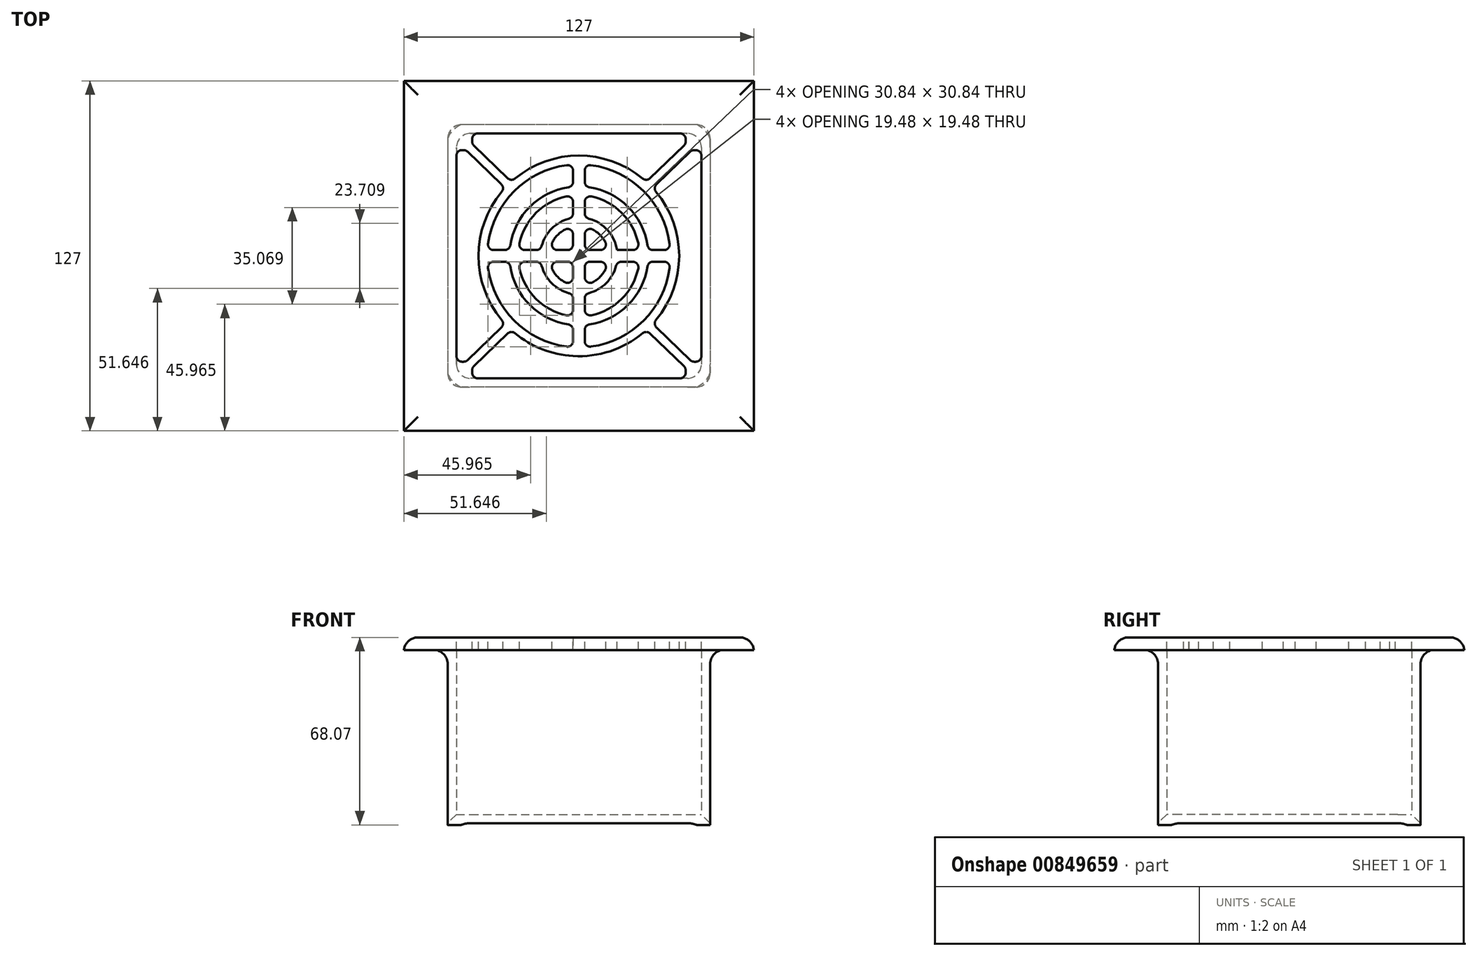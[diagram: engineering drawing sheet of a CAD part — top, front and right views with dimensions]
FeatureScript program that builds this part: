
annotation { "Feature Type Name" : "Feature", "Feature Type Description" : "" }
export const myFeature = defineFeature(function(context is Context, id is Id, definition is map)
    precondition{}
    {
        {
            var Q0;
            Q0=qCreatedBy(makeId("Top.planeOp"),FACE);
            var sketch = newSketch(context, id + "F0", { "sketchPlane" : qUnion([Q0])});
            skLineSegment(sketch, "E0.bottom", {"start": v(44.45, 44.45) * mm, "end": v(-44.45, 44.45) * mm});
            skLineSegment(sketch, "E0.top", {"start": v(44.45, -44.45) * mm, "end": v(-44.45, -44.45) * mm});
            skLineSegment(sketch, "E0.left", {"start": v(44.45, 44.45) * mm, "end": v(44.45, -44.45) * mm});
            skLineSegment(sketch, "E0.right", {"start": v(-44.45, 44.45) * mm, "end": v(-44.45, -44.45) * mm});
            skPoint(sketch, "E0.middle", {"position": v(0, 0) * mm});
            skLineSegment(sketch, "E1.0", {"start": v(47.63, 47.62) * mm, "end": v(-47.62, 47.62) * mm});
            skLineSegment(sketch, "E1.1", {"start": v(47.63, 47.62) * mm, "end": v(47.63, -47.62) * mm});
            skLineSegment(sketch, "E1.2", {"start": v(47.63, -47.62) * mm, "end": v(-47.62, -47.62) * mm});
            skLineSegment(sketch, "E1.3", {"start": v(-47.62, 47.62) * mm, "end": v(-47.62, -47.62) * mm});
            skSolve(sketch);
        }
        {
            var Q0;
            Q0=makeQuery(id+"F0.imprint","IMPRINT",FACE,{"disambiguationData":[TD([[makeQuery(id+"F0.imprint","IMPRINT",EDGE,{"derivedFrom":sQuery(id+"F0.wireOp",EDGE,"E0.bottom")}),-1.0]])]});
            extrude(context, id + "F1", {"entities" : qUnion([Q0]), "depth" : 63.5 * mm, "offsetDistance" : 25.4 * mm});
        }
        {
            var Q0;
            Q0=makeQuery(id+"F1.opExtrude","CAP_FACE",FACE,{"disambiguationData":[OSD([sQuery(id+"F0.wireOp",EDGE,"E0.bottom"),sQuery(id+"F0.wireOp",EDGE,"E0.top"),sQuery(id+"F0.wireOp",EDGE,"E0.left"),sQuery(id+"F0.wireOp",EDGE,"E0.right"),sQuery(id+"F0.wireOp",EDGE,"E1.0"),sQuery(id+"F0.wireOp",EDGE,"E1.1"),sQuery(id+"F0.wireOp",EDGE,"E1.2"),sQuery(id+"F0.wireOp",EDGE,"E1.3")])],"isStart":false});
            var sketch = newSketch(context, id + "F2", { "sketchPlane" : qUnion([Q0])});
            skLineSegment(sketch, "E2.bottom", {"start": v(63.5, 63.5) * mm, "end": v(-63.5, 63.5) * mm});
            skLineSegment(sketch, "E2.top", {"start": v(63.5, -63.5) * mm, "end": v(-63.5, -63.5) * mm});
            skLineSegment(sketch, "E2.left", {"start": v(63.5, 63.5) * mm, "end": v(63.5, -63.5) * mm});
            skLineSegment(sketch, "E2.right", {"start": v(-63.5, 63.5) * mm, "end": v(-63.5, -63.5) * mm});
            skPoint(sketch, "E2.middle", {"position": v(0, 0) * mm});
            skSolve(sketch);
        }
        {
            var Q0;
            Q0 = qSketchRegion(id + "F2", true);
            extrude(context, id + "F3", {"entities" : qUnion([Q0]), "operationType" : NewBodyOperationType.ADD, "depth" : 4.57 * mm, "offsetDistance" : 25.4 * mm});
        }
        {
            var Q0;
            Q0=makeQuery(id+"F3.opExtrude","CAP_FACE",FACE,{"disambiguationData":[OSD([sQuery(id+"F2.wireOp",EDGE,"E2.bottom"),sQuery(id+"F2.wireOp",EDGE,"E2.top"),sQuery(id+"F2.wireOp",EDGE,"E2.left"),sQuery(id+"F2.wireOp",EDGE,"E2.right")])],"isStart":false});
            var sketch = newSketch(context, id + "F4", { "sketchPlane" : qUnion([Q0])});
            skPoint(sketch, "E3.middle", {"position": v(0, 0) * mm});
            skArc(sketch, "E4", {"start": v(26.78, -24.66) * mm, "mid": v(36.4, 0) * mm, "end": v(26.78, 24.66) * mm});
            skLineSegment(sketch, "E5", {"start": v(-2.12, 2.12) * mm, "end": v(-2.12, 21.92) * mm});
            skLineSegment(sketch, "E6", {"start": v(-2.12, 33.16) * mm, "end": v(-2.12, 25.1) * mm});
            skLineSegment(sketch, "E7", {"start": v(-2.12, 2.12) * mm, "end": v(-10.6, 2.12) * mm});
            skLineSegment(sketch, "E8", {"start": v(-2.12, -2.12) * mm, "end": v(-10.6, -2.12) * mm});
            skLineSegment(sketch, "E9", {"start": v(33.16, 2.12) * mm, "end": v(25.1, 2.12) * mm});
            skLineSegment(sketch, "E10", {"start": v(2.12, -2.12) * mm, "end": v(10.6, -2.12) * mm});
            skLineSegment(sketch, "E11", {"start": v(36.4, -2.12) * mm, "end": v(36.35, -2.12) * mm});
            skLineSegment(sketch, "E12", {"start": v(2.12, -33.16) * mm, "end": v(2.12, -25.1) * mm});
            skLineSegment(sketch, "E13", {"start": v(-2.12, -2.12) * mm, "end": v(-2.12, -10.6) * mm});
            skLineSegment(sketch, "E14", {"start": v(-2.12, -36.4) * mm, "end": v(-2.1, -36.35) * mm});
            skLineSegment(sketch, "E15", {"start": v(2.12, 33.16) * mm, "end": v(2.12, 25.1) * mm});
            skPoint(sketch, "E16.orphan", {"position": v(0, 36.4) * mm});
            skPoint(sketch, "E17.orphan", {"position": v(36.4, 0) * mm});
            skPoint(sketch, "E18.orphan", {"position": v(-36.4, 0) * mm});
            skPoint(sketch, "E19.trimOffspring.end.orphan", {"position": v(0, -36.4) * mm});
            skArc(sketch, "E20", {"start": v(-2.12, 33.16) * mm, "mid": v(-23.5, 23.5) * mm, "end": v(-33.16, 2.12) * mm});
            skArc(sketch, "E21", {"start": v(-2.12, 25.1) * mm, "mid": v(-17.82, 17.82) * mm, "end": v(-25.1, 2.12) * mm});
            skArc(sketch, "E22", {"start": v(-2.12, 21.92) * mm, "mid": v(-15.57, 15.57) * mm, "end": v(-21.92, 2.12) * mm});
            skArc(sketch, "E23", {"start": v(-2.12, 13.83) * mm, "mid": v(-14, 0) * mm, "end": v(-2.12, -13.83) * mm});
            skPoint(sketch, "E24.orphan", {"position": v(2.12, 36.35) * mm});
            skLineSegment(sketch, "E25.trimOffspring", {"start": v(2.12, 21.92) * mm, "end": v(2.12, 13.83) * mm});
            skLineSegment(sketch, "E26.trimOffspring", {"start": v(-2.12, 21.92) * mm, "end": v(-2.12, 13.83) * mm});
            skLineSegment(sketch, "E27.trimOffspring", {"start": v(-2.12, 25.1) * mm, "end": v(-2.12, 33.16) * mm});
            skArc(sketch, "E28.trimOffspring", {"start": v(13.83, 2.12) * mm, "mid": v(9.9, 9.9) * mm, "end": v(2.12, 13.83) * mm});
            skArc(sketch, "E29.trimOffspring", {"start": v(21.92, 2.12) * mm, "mid": v(15.57, 15.57) * mm, "end": v(2.12, 21.92) * mm});
            skArc(sketch, "E30.trimOffspring", {"start": v(25.1, 2.12) * mm, "mid": v(17.82, 17.82) * mm, "end": v(2.12, 25.1) * mm});
            skArc(sketch, "E31.trimOffspring", {"start": v(33.16, 2.12) * mm, "mid": v(23.5, 23.5) * mm, "end": v(2.12, 33.16) * mm});
            skArc(sketch, "E32.trimOffspring", {"start": v(2.12, -25.1) * mm, "mid": v(17.82, -17.82) * mm, "end": v(25.1, -2.12) * mm});
            skArc(sketch, "E33.trimOffspring", {"start": v(2.12, -21.92) * mm, "mid": v(15.57, -15.57) * mm, "end": v(21.92, -2.12) * mm});
            skArc(sketch, "E34.trimOffspring", {"start": v(2.12, -13.83) * mm, "mid": v(9.9, -9.9) * mm, "end": v(13.83, -2.12) * mm});
            skArc(sketch, "E35.trimOffspring", {"start": v(2.12, -33.16) * mm, "mid": v(23.5, -23.5) * mm, "end": v(33.16, -2.12) * mm});
            skArc(sketch, "E36.trimOffspring", {"start": v(-33.16, -2.12) * mm, "mid": v(-23.5, -23.5) * mm, "end": v(-2.12, -33.16) * mm});
            skArc(sketch, "E37.trimOffspring", {"start": v(-25.1, -2.12) * mm, "mid": v(-17.82, -17.82) * mm, "end": v(-2.12, -25.1) * mm});
            skArc(sketch, "E38.trimOffspring", {"start": v(-21.92, -2.12) * mm, "mid": v(-15.57, -15.57) * mm, "end": v(-2.12, -21.92) * mm});
            skArc(sketch, "E39", {"start": v(-10.6, -2.12) * mm, "mid": v(0, -10.82) * mm, "end": v(10.6, -2.12) * mm});
            skArc(sketch, "E40.trimOffspring", {"start": v(10.6, 2.12) * mm, "mid": v(7.65, 7.65) * mm, "end": v(2.12, 10.6) * mm});
            skArc(sketch, "E41.trimOffspring", {"start": v(-2.12, 10.6) * mm, "mid": v(-7.65, 7.65) * mm, "end": v(-10.6, 2.12) * mm});
            skLineSegment(sketch, "E42.trimOffspring", {"start": v(2.12, 10.6) * mm, "end": v(2.12, 2.12) * mm});
            skLineSegment(sketch, "E43.trimOffspring", {"start": v(-2.12, 10.6) * mm, "end": v(-2.12, 2.12) * mm});
            skLineSegment(sketch, "E44.trimOffspring", {"start": v(-13.83, 2.12) * mm, "end": v(-21.92, 2.12) * mm});
            skLineSegment(sketch, "E45.trimOffspring", {"start": v(-13.83, -2.12) * mm, "end": v(-21.92, -2.12) * mm});
            skLineSegment(sketch, "E46.trimOffspring", {"start": v(-2.12, -13.83) * mm, "end": v(-2.12, -21.92) * mm});
            skLineSegment(sketch, "E47.trimOffspring", {"start": v(2.12, -10.6) * mm, "end": v(2.12, -2.12) * mm});
            skLineSegment(sketch, "E48.trimOffspring", {"start": v(10.6, -2.12) * mm, "end": v(2.12, -2.12) * mm});
            skLineSegment(sketch, "E49.trimOffspring", {"start": v(10.6, 2.12) * mm, "end": v(2.12, 2.12) * mm});
            skLineSegment(sketch, "E50.trimOffspring", {"start": v(-25.1, 2.12) * mm, "end": v(-33.16, 2.12) * mm});
            skLineSegment(sketch, "E51.trimOffspring", {"start": v(-25.1, -2.12) * mm, "end": v(-33.16, -2.12) * mm});
            skLineSegment(sketch, "E52.trimOffspring", {"start": v(-2.12, -25.1) * mm, "end": v(-2.12, -33.16) * mm});
            skLineSegment(sketch, "E53.trimOffspring", {"start": v(2.12, -21.92) * mm, "end": v(2.12, -13.83) * mm});
            skLineSegment(sketch, "E54.trimOffspring", {"start": v(21.92, -2.12) * mm, "end": v(13.83, -2.12) * mm});
            skLineSegment(sketch, "E55.trimOffspring", {"start": v(21.92, 2.12) * mm, "end": v(13.83, 2.12) * mm});
            skLineSegment(sketch, "E56.trimOffspring", {"start": v(25.1, -2.12) * mm, "end": v(33.16, -2.12) * mm});
            skLineSegment(sketch, "E57.trimOffspring", {"start": v(-2.12, -36.35) * mm, "end": v(-2.12, -36.4) * mm});
            skPoint(sketch, "E58.orphan", {"position": v(2.12, -36.35) * mm});
            skLineSegment(sketch, "E59.trimOffspring", {"start": v(13.83, -2.12) * mm, "end": v(21.92, -2.12) * mm});
            skLineSegment(sketch, "E60.trimOffspring", {"start": v(36.35, -2.12) * mm, "end": v(36.4, -2.12) * mm});
            skPoint(sketch, "E61.orphan", {"position": v(36.35, 2.12) * mm});
            skLineSegment(sketch, "E62.trimOffspring", {"start": v(33.16, -2.12) * mm, "end": v(25.1, -2.12) * mm});
            skLineSegment(sketch, "E63", {"start": v(-41, -38.4) * mm, "end": v(-26.78, -24.66) * mm});
            skLineSegment(sketch, "E64", {"start": v(-38.74, -40.64) * mm, "end": v(-24.53, -26.9) * mm});
            skLineSegment(sketch, "E65", {"start": v(0, 10.6) * mm, "end": v(0, -2.12) * mm, "construction": true});
            skLineSegment(sketch, "E66", {"start": v(0, 0) * mm, "end": v(9.6, 0) * mm, "construction": true});
            skLineSegment(sketch, "E67.MirrorCS", {"start": v(41, -38.4) * mm, "end": v(26.78, -24.66) * mm});
            skLineSegment(sketch, "E68.MirrorCS", {"start": v(38.74, -40.64) * mm, "end": v(24.53, -26.9) * mm});
            skLineSegment(sketch, "E69.MirrorCS", {"start": v(-38.73, 40.64) * mm, "end": v(-24.53, 26.9) * mm});
            skLineSegment(sketch, "E70.MirrorCS", {"start": v(-41, 38.4) * mm, "end": v(-26.78, 24.66) * mm});
            skLineSegment(sketch, "E71.MirrorCS", {"start": v(41, 38.4) * mm, "end": v(26.78, 24.66) * mm});
            skLineSegment(sketch, "E72.MirrorCS", {"start": v(38.74, 40.64) * mm, "end": v(24.53, 26.9) * mm});
            skArc(sketch, "E73.trimOffspring", {"start": v(-24.53, -26.9) * mm, "mid": v(0, -36.4) * mm, "end": v(24.53, -26.9) * mm});
            skArc(sketch, "E74.trimOffspring", {"start": v(-26.78, 24.66) * mm, "mid": v(-36.4, 0) * mm, "end": v(-26.78, -24.66) * mm});
            skArc(sketch, "E75.trimOffspring", {"start": v(24.53, 26.9) * mm, "mid": v(0, 36.4) * mm, "end": v(-24.53, 26.9) * mm});
            skLineSegment(sketch, "E76.bottom", {"start": v(-44.45, -44.45) * mm, "end": v(44.45, -44.45) * mm});
            skLineSegment(sketch, "E76.top", {"start": v(-44.45, 44.45) * mm, "end": v(44.45, 44.45) * mm});
            skLineSegment(sketch, "E76.left", {"start": v(-44.45, -44.45) * mm, "end": v(-44.45, 44.45) * mm});
            skLineSegment(sketch, "E76.right", {"start": v(44.45, -44.45) * mm, "end": v(44.45, 44.45) * mm});
            skLineSegment(sketch, "E77", {"start": v(38.74, -40.64) * mm, "end": v(38.74, -44.45) * mm});
            skLineSegment(sketch, "E78", {"start": v(41, -38.4) * mm, "end": v(44.45, -38.4) * mm});
            skLineSegment(sketch, "E79", {"start": v(38.74, 40.64) * mm, "end": v(38.74, 44.45) * mm});
            skLineSegment(sketch, "E80", {"start": v(41, 38.4) * mm, "end": v(44.45, 38.4) * mm});
            skLineSegment(sketch, "E81", {"start": v(-38.73, 40.64) * mm, "end": v(-38.73, 44.45) * mm});
            skLineSegment(sketch, "E82", {"start": v(-41, 38.4) * mm, "end": v(-44.45, 38.4) * mm});
            skLineSegment(sketch, "E83", {"start": v(-41, -38.4) * mm, "end": v(-44.45, -38.4) * mm});
            skLineSegment(sketch, "E84", {"start": v(-38.74, -40.64) * mm, "end": v(-38.74, -44.45) * mm});
            skSolve(sketch);
        }
        {
            var Q0;
            {var subQ2=sQuery(id+"F4.wireOp",EDGE,"E69.MirrorCS");Q0=makeQuery(id+"F4.imprint","IMPRINT",FACE,{"disambiguationData":[TD([[makeQuery(id+"F4.imprint","IMPRINT",EDGE,{"derivedFrom":subQ2}),1.0]])]});}
            var Q1;
            {var subQ0=sQuery(id+"F4.wireOp",EDGE,"E63");Q1=makeQuery(id+"F4.imprint","IMPRINT",FACE,{"disambiguationData":[TD([[makeQuery(id+"F4.imprint","IMPRINT",EDGE,{"derivedFrom":subQ0}),1.0]])]});}
            var Q2;
            Q2=makeQuery(id+"F4.imprint","IMPRINT",FACE,{"disambiguationData":[TD([[makeQuery(id+"F4.imprint","IMPRINT",EDGE,{"derivedFrom":sQuery(id+"F4.wireOp",EDGE,"E20")}),1.0]])]});
            var Q3;
            Q3=makeQuery(id+"F4.imprint","IMPRINT",FACE,{"disambiguationData":[TD([[makeQuery(id+"F4.imprint","IMPRINT",EDGE,{"derivedFrom":sQuery(id+"F4.wireOp",EDGE,"E22")}),1.0]])]});
            var Q4;
            Q4=makeQuery(id+"F4.imprint","IMPRINT",FACE,{"disambiguationData":[TD([[makeQuery(id+"F4.imprint","IMPRINT",EDGE,{"derivedFrom":sQuery(id+"F4.wireOp",EDGE,"E7")}),-1.0]])]});
            var Q5;
            Q5=makeQuery(id+"F4.imprint","IMPRINT",FACE,{"disambiguationData":[TD([[makeQuery(id+"F4.imprint","IMPRINT",EDGE,{"derivedFrom":sQuery(id+"F4.wireOp",EDGE,"E40.trimOffspring")}),1.0]])]});
            var Q6;
            {var subQ2=sQuery(id+"F4.wireOp",EDGE,"E47.trimOffspring");Q6=makeQuery(id+"F4.imprint","IMPRINT",FACE,{"disambiguationData":[TD([[makeQuery(id+"F4.imprint","IMPRINT",EDGE,{"derivedFrom":subQ2}),-1.0]])]});}
            var Q7;
            {var subQ0=sQuery(id+"F4.wireOp",EDGE,"E8");Q7=makeQuery(id+"F4.imprint","IMPRINT",FACE,{"disambiguationData":[TD([[makeQuery(id+"F4.imprint","IMPRINT",EDGE,{"derivedFrom":subQ0}),1.0]])]});}
            var Q8;
            Q8=makeQuery(id+"F4.imprint","IMPRINT",FACE,{"disambiguationData":[TD([[makeQuery(id+"F4.imprint","IMPRINT",EDGE,{"derivedFrom":sQuery(id+"F4.wireOp",EDGE,"E38.trimOffspring")}),1.0]])]});
            var Q9;
            Q9=makeQuery(id+"F4.imprint","IMPRINT",FACE,{"disambiguationData":[TD([[makeQuery(id+"F4.imprint","IMPRINT",EDGE,{"derivedFrom":sQuery(id+"F4.wireOp",EDGE,"E36.trimOffspring")}),1.0]])]});
            var Q10;
            {var subQ1=sQuery(id+"F4.wireOp",EDGE,"E14");Q10=makeQuery(id+"F4.imprint","IMPRINT",FACE,{"disambiguationData":[TD([[makeQuery(id+"F4.imprint","IMPRINT",EDGE,{"derivedFrom":subQ1}),-1.0]])]});}
            var Q11;
            Q11=makeQuery(id+"F4.imprint","IMPRINT",FACE,{"disambiguationData":[TD([[makeQuery(id+"F4.imprint","IMPRINT",EDGE,{"derivedFrom":sQuery(id+"F4.wireOp",EDGE,"E12")}),-1.0]])]});
            var Q12;
            Q12=makeQuery(id+"F4.imprint","IMPRINT",FACE,{"disambiguationData":[TD([[makeQuery(id+"F4.imprint","IMPRINT",EDGE,{"derivedFrom":sQuery(id+"F4.wireOp",EDGE,"E33.trimOffspring")}),1.0]])]});
            var Q13;
            {var subQ0=sQuery(id+"F4.wireOp",EDGE,"E67.MirrorCS");Q13=makeQuery(id+"F4.imprint","IMPRINT",FACE,{"disambiguationData":[TD([[makeQuery(id+"F4.imprint","IMPRINT",EDGE,{"derivedFrom":subQ0}),-1.0]])]});}
            var Q14;
            Q14=makeQuery(id+"F4.imprint","IMPRINT",FACE,{"disambiguationData":[TD([[makeQuery(id+"F4.imprint","IMPRINT",EDGE,{"derivedFrom":sQuery(id+"F4.wireOp",EDGE,"E9")}),-1.0]])]});
            var Q15;
            Q15=makeQuery(id+"F4.imprint","IMPRINT",FACE,{"disambiguationData":[TD([[makeQuery(id+"F4.imprint","IMPRINT",EDGE,{"derivedFrom":sQuery(id+"F4.wireOp",EDGE,"E25.trimOffspring")}),1.0]])]});
            extrude(context, id + "F5", {"entities" : qUnion([Q0, Q1, Q2, Q3, Q4, Q5, Q6, Q7, Q8, Q9, Q10, Q11, Q12, Q13, Q14, Q15]), "operationType" : NewBodyOperationType.REMOVE, "endBound" : BoundingType.THROUGH_ALL, "oppositeDirection" : true, "depth" : 25.4 * mm, "offsetDistance" : 25.4 * mm});
        }
        {
            var Q0;
            Q0=makeQuery(id+"F1.opExtrude","SWEPT_EDGE",EDGE,{"disambiguationData":[OSD([sQuery(id+"F0.wireOp",EDGE,"E1.0"),sQuery(id+"F0.wireOp",EDGE,"E1.1")])]});
            var Q1;
            Q1=makeQuery(id+"F1.opExtrude","SWEPT_EDGE",EDGE,{"disambiguationData":[OSD([sQuery(id+"F0.wireOp",EDGE,"E1.1"),sQuery(id+"F0.wireOp",EDGE,"E1.2")])]});
            var Q2;
            Q2=makeQuery(id+"F1.opExtrude","SWEPT_EDGE",EDGE,{"disambiguationData":[OSD([sQuery(id+"F0.wireOp",EDGE,"E1.0"),sQuery(id+"F0.wireOp",EDGE,"E1.3")])]});
            var Q3;
            Q3=makeQuery(id+"F3.opExtrude","CAP_EDGE",EDGE,{"disambiguationData":[OSD([sQuery(id+"F2.wireOp",EDGE,"E2.bottom")])],"isStart":false});
            var Q4;
            Q4=makeQuery(id+"F3.opExtrude","CAP_EDGE",EDGE,{"disambiguationData":[OSD([sQuery(id+"F2.wireOp",EDGE,"E2.left")])],"isStart":false});
            var Q5;
            Q5=makeQuery(id+"F3.opExtrude","CAP_EDGE",EDGE,{"disambiguationData":[OSD([sQuery(id+"F2.wireOp",EDGE,"E2.top")])],"isStart":false});
            var Q6;
            Q6=makeQuery(id+"F3.opExtrude","CAP_EDGE",EDGE,{"disambiguationData":[OSD([sQuery(id+"F2.wireOp",EDGE,"E2.right")])],"isStart":false});
            var Q7;
            Q7=makeQuery(id+"F1.opExtrude","SWEPT_EDGE",EDGE,{"disambiguationData":[OSD([sQuery(id+"F0.wireOp",EDGE,"E1.2"),sQuery(id+"F0.wireOp",EDGE,"E1.3")])]});
            var Q8;
            Q8=makeQuery(id+"F1.opExtrude","SWEPT_EDGE",EDGE,{"disambiguationData":[OSD([sQuery(id+"F0.wireOp",EDGE,"E0.bottom"),sQuery(id+"F0.wireOp",EDGE,"E0.right")])]});
            var Q9;
            Q9=makeQuery(id+"F1.opExtrude","SWEPT_EDGE",EDGE,{"disambiguationData":[OSD([sQuery(id+"F0.wireOp",EDGE,"E0.bottom"),sQuery(id+"F0.wireOp",EDGE,"E0.left")])]});
            var Q10;
            Q10=makeQuery(id+"F1.opExtrude","SWEPT_EDGE",EDGE,{"disambiguationData":[OSD([sQuery(id+"F0.wireOp",EDGE,"E0.top"),sQuery(id+"F0.wireOp",EDGE,"E0.left")])]});
            var Q11;
            Q11=makeQuery(id+"F1.opExtrude","SWEPT_EDGE",EDGE,{"disambiguationData":[OSD([sQuery(id+"F0.wireOp",EDGE,"E0.top"),sQuery(id+"F0.wireOp",EDGE,"E0.right")])]});
            fillet(context, id + "F6", {"entities" : qUnion([Q0, Q1, Q2, Q3, Q4, Q5, Q6, Q7, Q8, Q9, Q10, Q11]), "radius" : 5.08 * mm, "tangentPropagation" : true, "allowEdgeOverflow" : false});
        }
        {
            var Q0;
            Q0=makeQuery(id+"F5.boolean.opBoolean","COPY",EDGE,{"derivedFrom":makeQuery(id+"F5.opExtrude","SWEPT_EDGE",EDGE,{"disambiguationData":[OSD([sQuery(id+"F4.wireOp",EDGE,"Ny9JORe7-v1Iw-XlhY-zKWl-hX9oo0s8yrxZ.bottom"),sQuery(id+"F4.wireOp",EDGE,"E69.MirrorCS")])]})});
            var Q1;
            Q1=makeQuery(id+"F5.boolean.opBoolean","COPY",EDGE,{"derivedFrom":makeQuery(id+"F5.opExtrude","SWEPT_EDGE",EDGE,{"disambiguationData":[OSD([sQuery(id+"F4.wireOp",EDGE,"Ny9JORe7-v1Iw-XlhY-zKWl-hX9oo0s8yrxZ.right"),sQuery(id+"F4.wireOp",EDGE,"dAVf5oIQ-o4t2-s2eZ-aQ3L-IrBFGNoMoMhc")])]})});
            var Q2;
            Q2=makeQuery(id+"F5.boolean.opBoolean","COPY",EDGE,{"derivedFrom":makeQuery(id+"F5.opExtrude","SWEPT_EDGE",EDGE,{"disambiguationData":[OSD([sQuery(id+"F4.wireOp",EDGE,"E69.MirrorCS"),sQuery(id+"F4.wireOp",EDGE,"E75.trimOffspring")])]})});
            var Q3;
            Q3=makeQuery(id+"F5.boolean.opBoolean","COPY",EDGE,{"derivedFrom":makeQuery(id+"F5.opExtrude","SWEPT_EDGE",EDGE,{"disambiguationData":[OSD([sQuery(id+"F4.wireOp",EDGE,"E70.MirrorCS"),sQuery(id+"F4.wireOp",EDGE,"E74.trimOffspring")])]})});
            var Q4;
            Q4=makeQuery(id+"F5.boolean.opBoolean","COPY",EDGE,{"derivedFrom":makeQuery(id+"F5.opExtrude","SWEPT_EDGE",EDGE,{"disambiguationData":[OSD([sQuery(id+"F4.wireOp",EDGE,"sGeT2VpK-1eNm-xAgm-dLhG-xnKGUjQJ5Pfv.left"),sQuery(id+"F4.wireOp",EDGE,"5TgPAB1L-Vj3l-HR86-uruZ-VLY5y7cgneCX")])]})});
            var Q5;
            Q5=makeQuery(id+"F5.boolean.opBoolean","COPY",EDGE,{"derivedFrom":makeQuery(id+"F5.opExtrude","SWEPT_EDGE",EDGE,{"disambiguationData":[OSD([sQuery(id+"F4.wireOp",EDGE,"Ny9JORe7-v1Iw-XlhY-zKWl-hX9oo0s8yrxZ.bottom"),sQuery(id+"F4.wireOp",EDGE,"sGeT2VpK-1eNm-xAgm-dLhG-xnKGUjQJ5Pfv.bottom"),sQuery(id+"F4.wireOp",EDGE,"E72.MirrorCS")])]})});
            var Q6;
            Q6=makeQuery(id+"F5.boolean.opBoolean","COPY",EDGE,{"derivedFrom":makeQuery(id+"F5.opExtrude","SWEPT_EDGE",EDGE,{"disambiguationData":[OSD([sQuery(id+"F4.wireOp",EDGE,"Ny9JORe7-v1Iw-XlhY-zKWl-hX9oo0s8yrxZ.left"),sQuery(id+"F4.wireOp",EDGE,"1b44b59b-9a32-4855-84bd-7fad8672f93b0.MirrorCS")])]})});
            var Q7;
            Q7=makeQuery(id+"F5.boolean.opBoolean","COPY",EDGE,{"derivedFrom":makeQuery(id+"F5.opExtrude","SWEPT_EDGE",EDGE,{"disambiguationData":[OSD([sQuery(id+"F4.wireOp",EDGE,"Ny9JORe7-v1Iw-XlhY-zKWl-hX9oo0s8yrxZ.right"),sQuery(id+"F4.wireOp",EDGE,"2dcaf949-3c9a-4964-9e04-0e700857f11a0.MirrorCS")])]})});
            var Q8;
            Q8=makeQuery(id+"F5.boolean.opBoolean","COPY",EDGE,{"derivedFrom":makeQuery(id+"F5.opExtrude","SWEPT_EDGE",EDGE,{"disambiguationData":[OSD([sQuery(id+"F4.wireOp",EDGE,"Ny9JORe7-v1Iw-XlhY-zKWl-hX9oo0s8yrxZ.top"),sQuery(id+"F4.wireOp",EDGE,"E64")])]})});
            var Q9;
            Q9=makeQuery(id+"F5.boolean.opBoolean","COPY",EDGE,{"derivedFrom":makeQuery(id+"F5.opExtrude","SWEPT_EDGE",EDGE,{"disambiguationData":[OSD([sQuery(id+"F4.wireOp",EDGE,"Ny9JORe7-v1Iw-XlhY-zKWl-hX9oo0s8yrxZ.top"),sQuery(id+"F4.wireOp",EDGE,"E68.MirrorCS")])]})});
            var Q10;
            Q10=makeQuery(id+"F5.boolean.opBoolean","COPY",EDGE,{"derivedFrom":makeQuery(id+"F5.opExtrude","SWEPT_EDGE",EDGE,{"disambiguationData":[OSD([sQuery(id+"F4.wireOp",EDGE,"E72.MirrorCS"),sQuery(id+"F4.wireOp",EDGE,"E75.trimOffspring")])]})});
            var Q11;
            Q11=makeQuery(id+"F5.boolean.opBoolean","COPY",EDGE,{"derivedFrom":makeQuery(id+"F5.opExtrude","SWEPT_EDGE",EDGE,{"disambiguationData":[OSD([sQuery(id+"F4.wireOp",EDGE,"E4"),sQuery(id+"F4.wireOp",EDGE,"E71.MirrorCS")])]})});
            var Q12;
            Q12=makeQuery(id+"F5.boolean.opBoolean","COPY",EDGE,{"derivedFrom":makeQuery(id+"F5.opExtrude","SWEPT_EDGE",EDGE,{"disambiguationData":[OSD([sQuery(id+"F4.wireOp",EDGE,"E4"),sQuery(id+"F4.wireOp",EDGE,"E67.MirrorCS")])]})});
            var Q13;
            Q13=makeQuery(id+"F5.boolean.opBoolean","COPY",EDGE,{"derivedFrom":makeQuery(id+"F5.opExtrude","SWEPT_EDGE",EDGE,{"disambiguationData":[OSD([sQuery(id+"F4.wireOp",EDGE,"E68.MirrorCS"),sQuery(id+"F4.wireOp",EDGE,"E73.trimOffspring")])]})});
            var Q14;
            Q14=makeQuery(id+"F5.boolean.opBoolean","COPY",EDGE,{"derivedFrom":makeQuery(id+"F5.opExtrude","SWEPT_EDGE",EDGE,{"disambiguationData":[OSD([sQuery(id+"F4.wireOp",EDGE,"E64"),sQuery(id+"F4.wireOp",EDGE,"E73.trimOffspring")])]})});
            var Q15;
            Q15=makeQuery(id+"F5.boolean.opBoolean","COPY",EDGE,{"derivedFrom":makeQuery(id+"F5.opExtrude","SWEPT_EDGE",EDGE,{"disambiguationData":[OSD([sQuery(id+"F4.wireOp",EDGE,"E63"),sQuery(id+"F4.wireOp",EDGE,"E74.trimOffspring")])]})});
            var Q16;
            Q16=makeQuery(id+"F5.boolean.opBoolean","COPY",EDGE,{"derivedFrom":makeQuery(id+"F5.opExtrude","SWEPT_EDGE",EDGE,{"disambiguationData":[OSD([sQuery(id+"F4.wireOp",EDGE,"E47.trimOffspring"),sQuery(id+"F4.wireOp",EDGE,"E48.trimOffspring")])]})});
            var Q17;
            Q17=makeQuery(id+"F5.boolean.opBoolean","COPY",EDGE,{"derivedFrom":makeQuery(id+"F5.opExtrude","SWEPT_EDGE",EDGE,{"disambiguationData":[OSD([sQuery(id+"F4.wireOp",EDGE,"E40.trimOffspring"),sQuery(id+"F4.wireOp",EDGE,"E42.trimOffspring")])]})});
            var Q18;
            Q18=makeQuery(id+"F5.boolean.opBoolean","COPY",EDGE,{"derivedFrom":makeQuery(id+"F5.opExtrude","SWEPT_EDGE",EDGE,{"disambiguationData":[OSD([sQuery(id+"F4.wireOp",EDGE,"E40.trimOffspring"),sQuery(id+"F4.wireOp",EDGE,"E49.trimOffspring")])]})});
            var Q19;
            Q19=makeQuery(id+"F5.boolean.opBoolean","COPY",EDGE,{"derivedFrom":makeQuery(id+"F5.opExtrude","SWEPT_EDGE",EDGE,{"disambiguationData":[OSD([sQuery(id+"F4.wireOp",EDGE,"E42.trimOffspring"),sQuery(id+"F4.wireOp",EDGE,"E49.trimOffspring")])]})});
            fillet(context, id + "F7", {"entities" : qUnion([Q0, Q1, Q2, Q3, Q4, Q5, Q6, Q7, Q8, Q9, Q10, Q11, Q12, Q13, Q14, Q15, Q16, Q17, Q18, Q19]), "radius" : 2 * mm, "tangentPropagation" : true, "allowEdgeOverflow" : false});
        }
        {
            var Q0;
            Q0=makeQuery(id+"F5.boolean.opBoolean","COPY",EDGE,{"derivedFrom":makeQuery(id+"F5.opExtrude","SWEPT_EDGE",EDGE,{"disambiguationData":[OSD([sQuery(id+"F4.wireOp",EDGE,"E39"),sQuery(id+"F4.wireOp",EDGE,"E48.trimOffspring")])]})});
            var Q1;
            Q1=makeQuery(id+"F5.boolean.opBoolean","COPY",EDGE,{"derivedFrom":makeQuery(id+"F5.opExtrude","SWEPT_EDGE",EDGE,{"disambiguationData":[OSD([sQuery(id+"F4.wireOp",EDGE,"E39"),sQuery(id+"F4.wireOp",EDGE,"E47.trimOffspring")])]})});
            var Q2;
            Q2=makeQuery(id+"F5.boolean.opBoolean","COPY",EDGE,{"derivedFrom":makeQuery(id+"F5.opExtrude","SWEPT_EDGE",EDGE,{"disambiguationData":[OSD([sQuery(id+"F4.wireOp",EDGE,"E8"),sQuery(id+"F4.wireOp",EDGE,"E13")])]})});
            fillet(context, id + "F8", {"entities" : qUnion([Q0, Q1, Q2]), "radius" : 2 * mm, "tangentPropagation" : true, "allowEdgeOverflow" : false});
        }
        {
            var Q0;
            Q0=makeQuery(id+"F5.boolean.opBoolean","COPY",EDGE,{"derivedFrom":makeQuery(id+"F5.opExtrude","SWEPT_EDGE",EDGE,{"disambiguationData":[OSD([sQuery(id+"F4.wireOp",EDGE,"E8"),sQuery(id+"F4.wireOp",EDGE,"E39")])]})});
            var Q1;
            Q1=makeQuery(id+"F5.boolean.opBoolean","COPY",EDGE,{"derivedFrom":makeQuery(id+"F5.opExtrude","SWEPT_EDGE",EDGE,{"disambiguationData":[OSD([sQuery(id+"F4.wireOp",EDGE,"E13"),sQuery(id+"F4.wireOp",EDGE,"E39")])]})});
            var Q2;
            Q2=makeQuery(id+"F5.boolean.opBoolean","COPY",EDGE,{"derivedFrom":makeQuery(id+"F5.opExtrude","SWEPT_EDGE",EDGE,{"disambiguationData":[OSD([sQuery(id+"F4.wireOp",EDGE,"E7"),sQuery(id+"F4.wireOp",EDGE,"E43.trimOffspring")])]})});
            var Q3;
            Q3=makeQuery(id+"F5.boolean.opBoolean","COPY",EDGE,{"derivedFrom":makeQuery(id+"F5.opExtrude","SWEPT_EDGE",EDGE,{"disambiguationData":[OSD([sQuery(id+"F4.wireOp",EDGE,"E7"),sQuery(id+"F4.wireOp",EDGE,"E41.trimOffspring")])]})});
            var Q4;
            Q4=makeQuery(id+"F5.boolean.opBoolean","COPY",EDGE,{"derivedFrom":makeQuery(id+"F5.opExtrude","SWEPT_EDGE",EDGE,{"disambiguationData":[OSD([sQuery(id+"F4.wireOp",EDGE,"E41.trimOffspring"),sQuery(id+"F4.wireOp",EDGE,"E43.trimOffspring")])]})});
            var Q5;
            Q5=makeQuery(id+"F5.boolean.opBoolean","COPY",EDGE,{"derivedFrom":makeQuery(id+"F5.opExtrude","SWEPT_EDGE",EDGE,{"disambiguationData":[OSD([sQuery(id+"F4.wireOp",EDGE,"E25.trimOffspring"),sQuery(id+"F4.wireOp",EDGE,"E28.trimOffspring")])]})});
            var Q6;
            Q6=makeQuery(id+"F5.boolean.opBoolean","COPY",EDGE,{"derivedFrom":makeQuery(id+"F5.opExtrude","SWEPT_EDGE",EDGE,{"disambiguationData":[OSD([sQuery(id+"F4.wireOp",EDGE,"E25.trimOffspring"),sQuery(id+"F4.wireOp",EDGE,"E29.trimOffspring")])]})});
            var Q7;
            Q7=makeQuery(id+"F5.boolean.opBoolean","COPY",EDGE,{"derivedFrom":makeQuery(id+"F5.opExtrude","SWEPT_EDGE",EDGE,{"disambiguationData":[OSD([sQuery(id+"F4.wireOp",EDGE,"E29.trimOffspring"),sQuery(id+"F4.wireOp",EDGE,"E55.trimOffspring")])]})});
            var Q8;
            Q8=makeQuery(id+"F5.boolean.opBoolean","COPY",EDGE,{"derivedFrom":makeQuery(id+"F5.opExtrude","SWEPT_EDGE",EDGE,{"disambiguationData":[OSD([sQuery(id+"F4.wireOp",EDGE,"E9"),sQuery(id+"F4.wireOp",EDGE,"E31.trimOffspring")])]})});
            var Q9;
            Q9=makeQuery(id+"F5.boolean.opBoolean","COPY",EDGE,{"derivedFrom":makeQuery(id+"F5.opExtrude","SWEPT_EDGE",EDGE,{"disambiguationData":[OSD([sQuery(id+"F4.wireOp",EDGE,"E21"),sQuery(id+"F4.wireOp",EDGE,"E27.trimOffspring")])]})});
            var Q10;
            Q10=makeQuery(id+"F5.boolean.opBoolean","COPY",EDGE,{"derivedFrom":makeQuery(id+"F5.opExtrude","SWEPT_EDGE",EDGE,{"disambiguationData":[OSD([sQuery(id+"F4.wireOp",EDGE,"E21"),sQuery(id+"F4.wireOp",EDGE,"E50.trimOffspring")])]})});
            var Q11;
            Q11=makeQuery(id+"F5.boolean.opBoolean","COPY",EDGE,{"derivedFrom":makeQuery(id+"F5.opExtrude","SWEPT_EDGE",EDGE,{"disambiguationData":[OSD([sQuery(id+"F4.wireOp",EDGE,"E23"),sQuery(id+"F4.wireOp",EDGE,"E44.trimOffspring")])]})});
            var Q12;
            Q12=makeQuery(id+"F5.boolean.opBoolean","COPY",EDGE,{"derivedFrom":makeQuery(id+"F5.opExtrude","SWEPT_EDGE",EDGE,{"disambiguationData":[OSD([sQuery(id+"F4.wireOp",EDGE,"E38.trimOffspring"),sQuery(id+"F4.wireOp",EDGE,"E46.trimOffspring")])]})});
            fillet(context, id + "F9", {"entities" : qUnion([Q0, Q1, Q2, Q3, Q4, Q5, Q6, Q7, Q8, Q9, Q10, Q11, Q12]), "radius" : 2 * mm, "tangentPropagation" : true, "allowEdgeOverflow" : false});
        }
        {
            var Q0;
            Q0=makeQuery(id+"F5.boolean.opBoolean","COPY",EDGE,{"derivedFrom":makeQuery(id+"F5.opExtrude","SWEPT_EDGE",EDGE,{"disambiguationData":[OSD([sQuery(id+"F4.wireOp",EDGE,"E15"),sQuery(id+"F4.wireOp",EDGE,"E31.trimOffspring")])]})});
            var Q1;
            Q1=makeQuery(id+"F5.boolean.opBoolean","COPY",EDGE,{"derivedFrom":makeQuery(id+"F5.opExtrude","SWEPT_EDGE",EDGE,{"disambiguationData":[OSD([sQuery(id+"F4.wireOp",EDGE,"E32.trimOffspring"),sQuery(id+"F4.wireOp",EDGE,"E62.trimOffspring")])]})});
            var Q2;
            Q2=makeQuery(id+"F5.boolean.opBoolean","COPY",EDGE,{"derivedFrom":makeQuery(id+"F5.opExtrude","SWEPT_EDGE",EDGE,{"disambiguationData":[OSD([sQuery(id+"F4.wireOp",EDGE,"E12"),sQuery(id+"F4.wireOp",EDGE,"E32.trimOffspring")])]})});
            var Q3;
            Q3=makeQuery(id+"F5.boolean.opBoolean","COPY",EDGE,{"derivedFrom":makeQuery(id+"F5.opExtrude","SWEPT_EDGE",EDGE,{"disambiguationData":[OSD([sQuery(id+"F4.wireOp",EDGE,"E34.trimOffspring"),sQuery(id+"F4.wireOp",EDGE,"E59.trimOffspring")])]})});
            var Q4;
            Q4=makeQuery(id+"F5.boolean.opBoolean","COPY",EDGE,{"derivedFrom":makeQuery(id+"F5.opExtrude","SWEPT_EDGE",EDGE,{"disambiguationData":[OSD([sQuery(id+"F4.wireOp",EDGE,"E34.trimOffspring"),sQuery(id+"F4.wireOp",EDGE,"E53.trimOffspring")])]})});
            var Q5;
            Q5=makeQuery(id+"F5.boolean.opBoolean","COPY",EDGE,{"derivedFrom":makeQuery(id+"F5.opExtrude","SWEPT_EDGE",EDGE,{"disambiguationData":[OSD([sQuery(id+"F4.wireOp",EDGE,"E9"),sQuery(id+"F4.wireOp",EDGE,"E30.trimOffspring")])]})});
            var Q6;
            Q6=makeQuery(id+"F5.boolean.opBoolean","COPY",EDGE,{"derivedFrom":makeQuery(id+"F5.opExtrude","SWEPT_EDGE",EDGE,{"disambiguationData":[OSD([sQuery(id+"F4.wireOp",EDGE,"E15"),sQuery(id+"F4.wireOp",EDGE,"E30.trimOffspring")])]})});
            fillet(context, id + "F10", {"entities" : qUnion([Q0, Q1, Q2, Q3, Q4, Q5, Q6]), "radius" : 2 * mm, "tangentPropagation" : true, "allowEdgeOverflow" : false});
        }
        {
            var Q0;
            Q0=makeQuery(id+"F5.boolean.opBoolean","COPY",EDGE,{"derivedFrom":makeQuery(id+"F5.opExtrude","SWEPT_EDGE",EDGE,{"disambiguationData":[OSD([sQuery(id+"F4.wireOp",EDGE,"E36.trimOffspring"),sQuery(id+"F4.wireOp",EDGE,"E52.trimOffspring")])]})});
            var Q1;
            Q1=makeQuery(id+"F5.boolean.opBoolean","COPY",EDGE,{"derivedFrom":makeQuery(id+"F5.opExtrude","SWEPT_EDGE",EDGE,{"disambiguationData":[OSD([sQuery(id+"F4.wireOp",EDGE,"E12"),sQuery(id+"F4.wireOp",EDGE,"E35.trimOffspring")])]})});
            var Q2;
            Q2=makeQuery(id+"F5.boolean.opBoolean","COPY",EDGE,{"derivedFrom":makeQuery(id+"F5.opExtrude","SWEPT_EDGE",EDGE,{"disambiguationData":[OSD([sQuery(id+"F4.wireOp",EDGE,"E37.trimOffspring"),sQuery(id+"F4.wireOp",EDGE,"E52.trimOffspring")])]})});
            var Q3;
            Q3=makeQuery(id+"F5.boolean.opBoolean","COPY",EDGE,{"derivedFrom":makeQuery(id+"F5.opExtrude","SWEPT_EDGE",EDGE,{"disambiguationData":[OSD([sQuery(id+"F4.wireOp",EDGE,"E35.trimOffspring"),sQuery(id+"F4.wireOp",EDGE,"E62.trimOffspring")])]})});
            var Q4;
            Q4=makeQuery(id+"F5.boolean.opBoolean","COPY",EDGE,{"derivedFrom":makeQuery(id+"F5.opExtrude","SWEPT_EDGE",EDGE,{"disambiguationData":[OSD([sQuery(id+"F4.wireOp",EDGE,"E36.trimOffspring"),sQuery(id+"F4.wireOp",EDGE,"E51.trimOffspring")])]})});
            var Q5;
            Q5=makeQuery(id+"F5.boolean.opBoolean","COPY",EDGE,{"derivedFrom":makeQuery(id+"F5.opExtrude","SWEPT_EDGE",EDGE,{"disambiguationData":[OSD([sQuery(id+"F4.wireOp",EDGE,"E20"),sQuery(id+"F4.wireOp",EDGE,"E50.trimOffspring")])]})});
            var Q6;
            Q6=makeQuery(id+"F5.boolean.opBoolean","COPY",EDGE,{"derivedFrom":makeQuery(id+"F5.opExtrude","SWEPT_EDGE",EDGE,{"disambiguationData":[OSD([sQuery(id+"F4.wireOp",EDGE,"E20"),sQuery(id+"F4.wireOp",EDGE,"E27.trimOffspring")])]})});
            var Q7;
            Q7=makeQuery(id+"F5.boolean.opBoolean","COPY",EDGE,{"derivedFrom":makeQuery(id+"F5.opExtrude","SWEPT_EDGE",EDGE,{"disambiguationData":[OSD([sQuery(id+"F4.wireOp",EDGE,"E23"),sQuery(id+"F4.wireOp",EDGE,"E45.trimOffspring")])]})});
            var Q8;
            Q8=makeQuery(id+"F5.boolean.opBoolean","COPY",EDGE,{"derivedFrom":makeQuery(id+"F5.opExtrude","SWEPT_EDGE",EDGE,{"disambiguationData":[OSD([sQuery(id+"F4.wireOp",EDGE,"E38.trimOffspring"),sQuery(id+"F4.wireOp",EDGE,"E45.trimOffspring")])]})});
            var Q9;
            Q9=makeQuery(id+"F5.boolean.opBoolean","COPY",EDGE,{"derivedFrom":makeQuery(id+"F5.opExtrude","SWEPT_EDGE",EDGE,{"disambiguationData":[OSD([sQuery(id+"F4.wireOp",EDGE,"E23"),sQuery(id+"F4.wireOp",EDGE,"E46.trimOffspring")])]})});
            var Q10;
            Q10=makeQuery(id+"F5.boolean.opBoolean","COPY",EDGE,{"derivedFrom":makeQuery(id+"F5.opExtrude","SWEPT_EDGE",EDGE,{"disambiguationData":[OSD([sQuery(id+"F4.wireOp",EDGE,"E33.trimOffspring"),sQuery(id+"F4.wireOp",EDGE,"E59.trimOffspring")])]})});
            var Q11;
            Q11=makeQuery(id+"F5.boolean.opBoolean","COPY",EDGE,{"derivedFrom":makeQuery(id+"F5.opExtrude","SWEPT_EDGE",EDGE,{"disambiguationData":[OSD([sQuery(id+"F4.wireOp",EDGE,"E33.trimOffspring"),sQuery(id+"F4.wireOp",EDGE,"E53.trimOffspring")])]})});
            var Q12;
            Q12=makeQuery(id+"F5.boolean.opBoolean","COPY",EDGE,{"derivedFrom":makeQuery(id+"F5.opExtrude","SWEPT_EDGE",EDGE,{"disambiguationData":[OSD([sQuery(id+"F4.wireOp",EDGE,"E37.trimOffspring"),sQuery(id+"F4.wireOp",EDGE,"E51.trimOffspring")])]})});
            fillet(context, id + "F11", {"entities" : qUnion([Q0, Q1, Q2, Q3, Q4, Q5, Q6, Q7, Q8, Q9, Q10, Q11, Q12]), "radius" : 2 * mm, "tangentPropagation" : true, "allowEdgeOverflow" : false});
        }
        {
            var Q0;
            Q0=makeQuery(id+"F5.boolean.opBoolean","COPY",EDGE,{"derivedFrom":makeQuery(id+"F5.opExtrude","SWEPT_EDGE",EDGE,{"disambiguationData":[OSD([sQuery(id+"F4.wireOp",EDGE,"E22"),sQuery(id+"F4.wireOp",EDGE,"E26.trimOffspring")])]})});
            var Q1;
            Q1=makeQuery(id+"F5.boolean.opBoolean","COPY",EDGE,{"derivedFrom":makeQuery(id+"F5.opExtrude","SWEPT_EDGE",EDGE,{"disambiguationData":[OSD([sQuery(id+"F4.wireOp",EDGE,"E23"),sQuery(id+"F4.wireOp",EDGE,"E26.trimOffspring")])]})});
            var Q2;
            Q2=makeQuery(id+"F5.boolean.opBoolean","COPY",EDGE,{"derivedFrom":makeQuery(id+"F5.opExtrude","SWEPT_EDGE",EDGE,{"disambiguationData":[OSD([sQuery(id+"F4.wireOp",EDGE,"E22"),sQuery(id+"F4.wireOp",EDGE,"E44.trimOffspring")])]})});
            fillet(context, id + "F12", {"entities" : qUnion([Q0, Q1, Q2]), "radius" : 2 * mm, "tangentPropagation" : true, "allowEdgeOverflow" : false});
        }
        {
            var Q0;
            Q0=makeQuery(id+"F1.opExtrude","CAP_EDGE",EDGE,{"disambiguationData":[OSD([sQuery(id+"F0.wireOp",EDGE,"E0.top")])],"isStart":true});
            chamfer(context, id + "F13", {"entities" : qUnion([Q0]), "width" : 3.8 * mm, "tangentPropagation" : true});
        }
        {
            var Q0;
            Q0=makeQuery(id+"F5.boolean.opBoolean","COPY",EDGE,{"derivedFrom":makeQuery(id+"F5.opExtrude","SWEPT_EDGE",EDGE,{"disambiguationData":[OSD([sQuery(id+"F4.wireOp",EDGE,"E67.MirrorCS"),sQuery(id+"F4.wireOp",EDGE,"E78")])]})});
            var Q1;
            Q1=makeQuery(id+"F5.boolean.opBoolean","COPY",EDGE,{"derivedFrom":makeQuery(id+"F5.opExtrude","SWEPT_EDGE",EDGE,{"disambiguationData":[OSD([sQuery(id+"F4.wireOp",EDGE,"E76.right"),sQuery(id+"F4.wireOp",EDGE,"E78")])]})});
            var Q2;
            Q2=makeQuery(id+"F5.boolean.opBoolean","COPY",EDGE,{"derivedFrom":makeQuery(id+"F5.opExtrude","SWEPT_EDGE",EDGE,{"disambiguationData":[OSD([sQuery(id+"F4.wireOp",EDGE,"E76.bottom"),sQuery(id+"F4.wireOp",EDGE,"E77")])]})});
            var Q3;
            Q3=makeQuery(id+"F5.boolean.opBoolean","COPY",EDGE,{"derivedFrom":makeQuery(id+"F5.opExtrude","SWEPT_EDGE",EDGE,{"disambiguationData":[OSD([sQuery(id+"F4.wireOp",EDGE,"E76.bottom"),sQuery(id+"F4.wireOp",EDGE,"E84")])]})});
            var Q4;
            Q4=makeQuery(id+"F5.boolean.opBoolean","COPY",EDGE,{"derivedFrom":makeQuery(id+"F5.opExtrude","SWEPT_EDGE",EDGE,{"disambiguationData":[OSD([sQuery(id+"F4.wireOp",EDGE,"E76.left"),sQuery(id+"F4.wireOp",EDGE,"E83")])]})});
            var Q5;
            Q5=makeQuery(id+"F5.boolean.opBoolean","COPY",EDGE,{"derivedFrom":makeQuery(id+"F5.opExtrude","SWEPT_EDGE",EDGE,{"disambiguationData":[OSD([sQuery(id+"F4.wireOp",EDGE,"E63"),sQuery(id+"F4.wireOp",EDGE,"E83")])]})});
            var Q6;
            Q6=makeQuery(id+"F5.boolean.opBoolean","COPY",EDGE,{"derivedFrom":makeQuery(id+"F5.opExtrude","SWEPT_EDGE",EDGE,{"disambiguationData":[OSD([sQuery(id+"F4.wireOp",EDGE,"E70.MirrorCS"),sQuery(id+"F4.wireOp",EDGE,"E82")])]})});
            var Q7;
            {var subQ0=sQuery(id+"F4.wireOp",EDGE,"E81");Q7=makeQuery(id+"F7.opFillet","BLEND_EDGE",EDGE,{"blendedFrom":[makeQuery(id+"F5.boolean.opBoolean","COPY",EDGE,{"derivedFrom":makeQuery(id+"F5.opExtrude","SWEPT_EDGE",EDGE,{"disambiguationData":[OSD([sQuery(id+"F4.wireOp",EDGE,"E69.MirrorCS"),subQ0])]})}),makeQuery(id+"F5.boolean.opBoolean","COPY",FACE,{"derivedFrom":makeQuery(id+"F5.opExtrude","SWEPT_FACE",FACE,{"disambiguationData":[OSD([subQ0])]})})],"blendedInto":[makeQuery(id+"F5.boolean.opBoolean","COPY",FACE,{"derivedFrom":makeQuery(id+"F5.opExtrude","SWEPT_FACE",FACE,{"disambiguationData":[OSD([subQ0])]})})]});}
            var Q8;
            Q8=makeQuery(id+"F5.boolean.opBoolean","COPY",EDGE,{"derivedFrom":makeQuery(id+"F5.opExtrude","SWEPT_EDGE",EDGE,{"disambiguationData":[OSD([sQuery(id+"F4.wireOp",EDGE,"E76.top"),sQuery(id+"F4.wireOp",EDGE,"E81")])]})});
            var Q9;
            Q9=makeQuery(id+"F5.boolean.opBoolean","COPY",EDGE,{"derivedFrom":makeQuery(id+"F5.opExtrude","SWEPT_EDGE",EDGE,{"disambiguationData":[OSD([sQuery(id+"F4.wireOp",EDGE,"E76.left"),sQuery(id+"F4.wireOp",EDGE,"E82")])]})});
            var Q10;
            Q10=makeQuery(id+"F5.boolean.opBoolean","COPY",EDGE,{"derivedFrom":makeQuery(id+"F5.opExtrude","SWEPT_EDGE",EDGE,{"disambiguationData":[OSD([sQuery(id+"F4.wireOp",EDGE,"E76.top"),sQuery(id+"F4.wireOp",EDGE,"E79")])]})});
            var Q11;
            Q11=makeQuery(id+"F5.boolean.opBoolean","COPY",EDGE,{"derivedFrom":makeQuery(id+"F5.opExtrude","SWEPT_EDGE",EDGE,{"disambiguationData":[OSD([sQuery(id+"F4.wireOp",EDGE,"E71.MirrorCS"),sQuery(id+"F4.wireOp",EDGE,"E80")])]})});
            var Q12;
            Q12=makeQuery(id+"F5.boolean.opBoolean","COPY",EDGE,{"derivedFrom":makeQuery(id+"F5.opExtrude","SWEPT_EDGE",EDGE,{"disambiguationData":[OSD([sQuery(id+"F4.wireOp",EDGE,"E76.right"),sQuery(id+"F4.wireOp",EDGE,"E80")])]})});
            fillet(context, id + "F14", {"entities" : qUnion([Q0, Q1, Q2, Q3, Q4, Q5, Q6, Q7, Q8, Q9, Q10, Q11, Q12]), "radius" : 2 * mm, "tangentPropagation" : true, "allowEdgeOverflow" : false});
        }
        {
            var Q0;
            Q0=makeQuery(id+"F1.opExtrude","CAP_EDGE",EDGE,{"disambiguationData":[OSD([sQuery(id+"F0.wireOp",EDGE,"E1.1")])],"isStart":false});
            fillet(context, id + "F15", {"entities" : qUnion([Q0]), "radius" : 5.08 * mm, "tangentPropagation" : true, "allowEdgeOverflow" : false});
        }
    });
